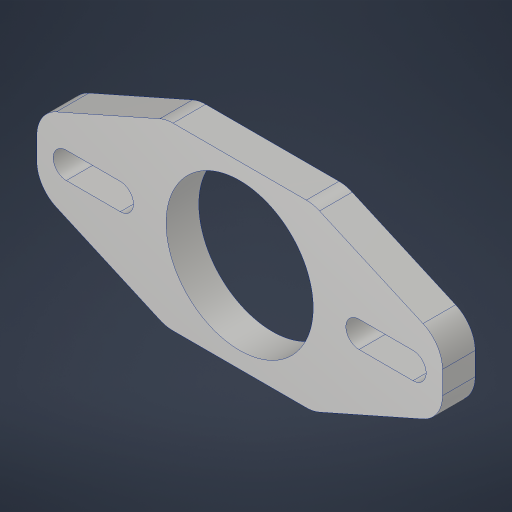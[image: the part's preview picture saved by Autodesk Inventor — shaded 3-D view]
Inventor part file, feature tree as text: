
AUTODESK INVENTOR PART (.ipt)
format: ipt  version: 2023.4 (Build 274418000, 418)  size: 229,376 bytes
history: native  units: in
note: dims shown in document units (in); Inventor stores cm internally (conversion verified against a paired STEP export)
features: extrude x1, fillet x1, plane x1, sketch x1
ambient origin geometry x8: Origin, YZ Plane, XZ Plane, XY Plane, X Axis, Y Axis, Z Axis, Center Point
bodies: Solid1 (feature_tree)
feature tree (4):
  extrude  "Extrusion1"  Depth=0.25in TaperAngle=0.0deg
  fillet  "Fillet1"  Radius=1.125in
  plane  "Work Plane1"
  sketch  "Sketch1"  dims[d0=1.125in d1=0.25in d2=0.0in d3=1.125in d4=0.125in d5=0.6875in d6=0.6875in d7=0.4125in d8=0.4125in d9=0.25in d10=0.201in d11=1.1193in d12=0.375in d13=1.074in d16=4.297in d19=1.432in d20=4.201in d21=2.0in d22=1.1193in d23=0.125in d24=0.2255in d25=0.2255in d26=0.5in d27=0.25in]
